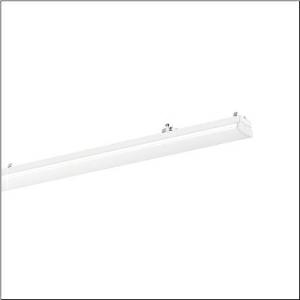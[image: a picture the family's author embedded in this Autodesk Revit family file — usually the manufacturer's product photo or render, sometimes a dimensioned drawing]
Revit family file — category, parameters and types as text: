
# Revit family: licross_r__11_recessed_opal_mo_51tl1d7n46xg_f8f9
name_source: partatom
category: Lighting Fixtures
units: mm (PartAtom-declared; Revit-internal decimal feet)

## family parameters
Cut with Voids When Loaded = No
Host = Face
Light Source = No
Part Type = Normal
Room Calculation Point = No
Round Connector Dimension = Use Diameter
Shared = No

## types (1)
- Licross® 11 recessed opal MO (1 x LED, 6300 lm, 35.1 W, 4000K)
    Apparent Load = 35 VA
    CIE Flux Codes = 44 73 91 87 100
    Color Rendering = 80
    Color Temperature = 4000K
    Default Elevation = 1800 mm
    Description = Licross® 11 recessed opal MO, luminaire insert, of sheet steel, coil coated, white, length: 1.500mm, width: 76mm, height: 87mm, LED rated luminous flux: 6.300lm, light colour: 840, control gear: ON/OFF, with plug, 3-pole, with phase selection, mains connection: 220..240V, AC, 50/60Hz, rated input power: 35W, halogen-free wiring, primary optical cover: cover, of PMMA, light emission: direct with ceiling illumination distribution, primary light characteristic: symmetric, protection rating (complete): IP40, insulation class (complete): insulation class I (protective earthing), certification: CE, ENEC, VDE, UKCA, protection symbol: D if used in an environment without relevant dust loads with corresponding accessories, impact resistance: IK06, permissible ambient temperature for indoor applications: -35..+45°C, corresponds to IFS (International Featured Standards) requirements for safety and quality in the food industry, reducing of maximum allowable ambient temperature of 5°C with ceiling mounting, packaging unit: 1 piece
    Height = 83 mm
    Lamp = 1 x LED
    Lamp Light Flux = 6300 lm
    Lamp Power = 35.1 W
    Lamp count = 1
    Length = 1500 mm
    Luminous efficacy = 179 lm/W
    Manufacturer = Siteco
    ModVariant = No
    Model = 51TL1D7N46XG
    Mounting Place = Ceiling
    Mounting Type = Pendant
    Number of Poles = 1
    OnlyDefault = Yes
    Power Factor = 1
    Product Name = Licross® 11 recessed opal MO
    Product group = luminaire insert
    ProductGroupID = 902
    Protection Class = Protection class I
    Protection Degree = IP 40
    RLX_Detail_Level = 1
    RLX_Emergency_Light_Flux = 0 lm
    RLX_Emergency_Type = 0
    RLX_Emergency_Type_DB = No
    RlxData = <blob elided: 23009 chars, md5=85b334fc>
    Socket = socket
    Standby Power = 0 W
    System Light Flux = 6300 lm
    System Power = 35 W
    Type Comments = Product without accessories
    Type Image = l_1313666.jpg
    URL = http://relux.com
    VarID = ---
    Voltage = 0 V
    Weight = 0.00 kg
    Width = 76 mm

## geometry (parser evidence)
native form markers: Blend x4, Sweep x11
no freeform markers — native parametric forms only
